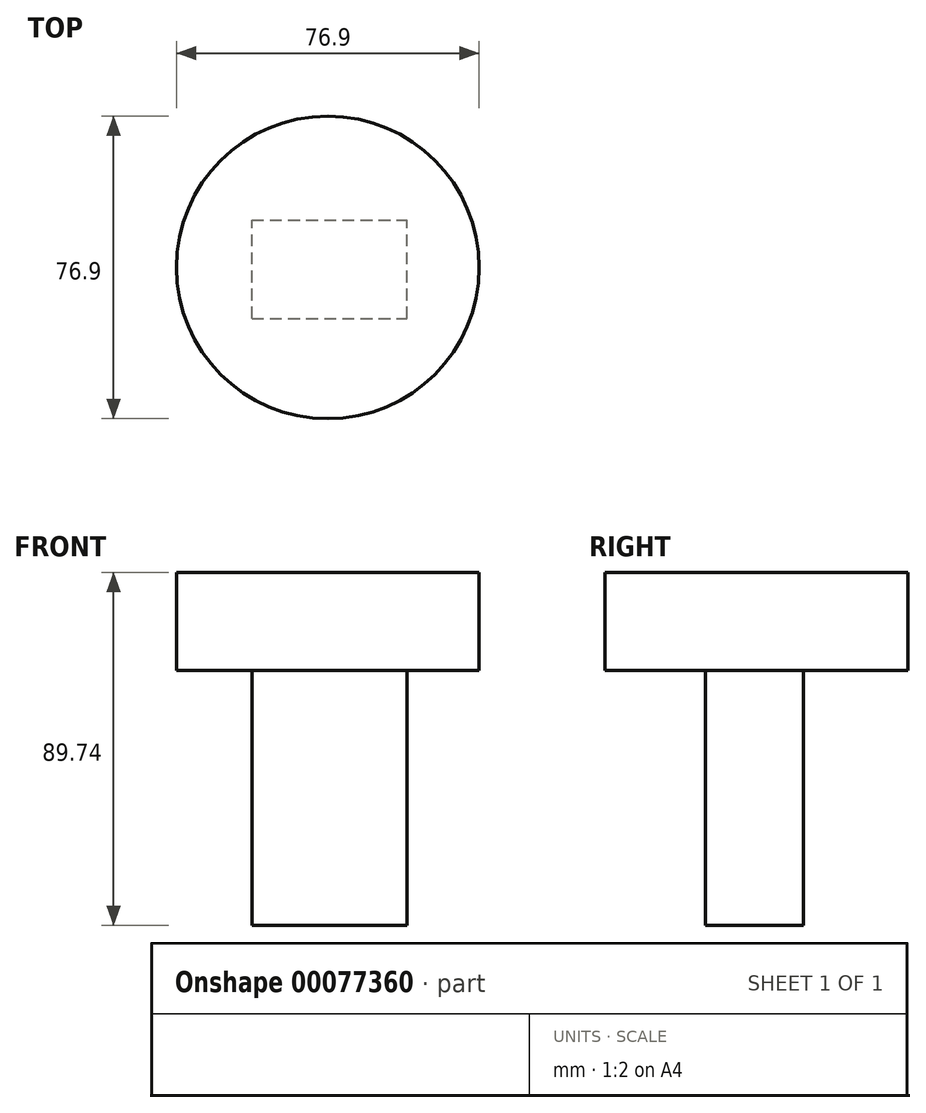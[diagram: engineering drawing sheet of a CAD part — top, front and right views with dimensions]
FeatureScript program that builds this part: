
annotation { "Feature Type Name" : "Feature", "Feature Type Description" : "" }
export const myFeature = defineFeature(function(context is Context, id is Id, definition is map)
    precondition{}
    {
        {
            var Q0;
            Q0=qCreatedBy(makeId("Front.planeOp"),FACE);
            var sketch = newSketch(context, id + "F0", { "sketchPlane" : qUnion([Q0])});
            skLineSegment(sketch, "E0.bottom", {"start": v(-19.29, 0) * mm, "end": v(20.1, 0) * mm});
            skLineSegment(sketch, "E0.top", {"start": v(-19.29, -64.74) * mm, "end": v(20.1, -64.74) * mm});
            skLineSegment(sketch, "E0.left", {"start": v(-19.29, 0) * mm, "end": v(-19.29, -64.74) * mm});
            skLineSegment(sketch, "E0.right", {"start": v(20.1, 0) * mm, "end": v(20.1, -64.74) * mm});
            skSolve(sketch);
        }
        {
            var Q0;
            Q0 = qSketchRegion(id + "F0", true);
            extrude(context, id + "F1", {"entities" : qUnion([Q0]), "depth" : 25 * mm});
        }
        {
            var Q0;
            Q0=qCreatedBy(makeId("Top.planeOp"),FACE);
            var sketch = newSketch(context, id + "F2", { "sketchPlane" : qUnion([Q0])});
            skCircle(sketch, "E1", {"center": v(0, -12) * mm, "radius": 38.45 * mm});
            skSolve(sketch);
        }
        {
            var Q0;
            Q0 = qSketchRegion(id + "F2", true);
            extrude(context, id + "F3", {"entities" : qUnion([Q0]), "operationType" : NewBodyOperationType.ADD, "depth" : 25 * mm});
        }
    });
